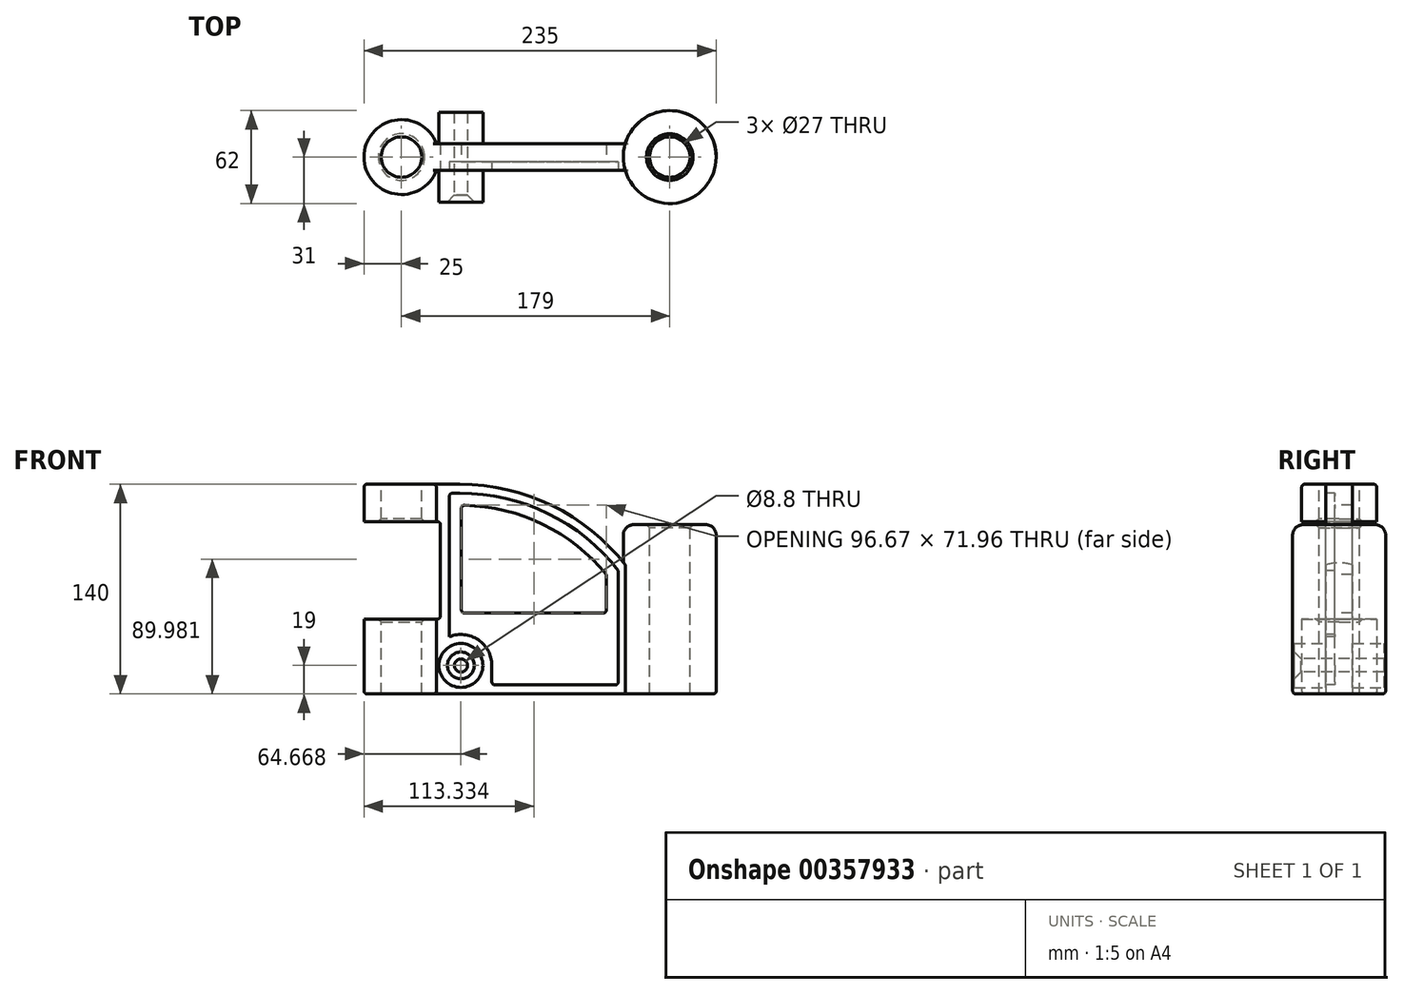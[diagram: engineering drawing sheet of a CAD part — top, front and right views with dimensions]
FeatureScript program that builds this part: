
annotation { "Feature Type Name" : "Feature", "Feature Type Description" : "" }
export const myFeature = defineFeature(function(context is Context, id is Id, definition is map)
    precondition{}
    {
        {
            assignVariable(context, id + "F0", {"name" : "A", "anyValue" : 140 * mm});
        }
        {
            assignVariable(context, id + "F1", {"name" : "B", "anyValue" : 62 * mm});
        }
        {
            assignVariable(context, id + "F2", {"name" : "Y", "anyValue" : (1.5 * getVariable(context, 'B')) + 20 * mm});
        }
        {
            var Q0;
            Q0=qCreatedBy(makeId("Top.planeOp"),FACE);
            var sketch = newSketch(context, id + "F3", { "sketchPlane" : qUnion([Q0])});
            skCircle(sketch, "E0", {"center": v(0, 0) * mm, "radius": 25 * mm});
            skSolve(sketch);
        }
        {
            var Q0;
            Q0 = qSketchRegion(id + "F3", true);
            extrude(context, id + "F4", {"entities" : qUnion([Q0]), "depth" : getVariable(context, 'A')});
        }
        {
            var Q0;
            Q0=qCreatedBy(makeId("Top.planeOp"),FACE);
            var sketch = newSketch(context, id + "F5", { "sketchPlane" : qUnion([Q0])});
            skCircle(sketch, "E1", {"center": v(179, 0) * mm, "radius": 31 * mm});
            skSolve(sketch);
        }
        {
            var Q0;
            Q0 = qSketchRegion(id + "F5", true);
            extrude(context, id + "F6", {"entities" : qUnion([Q0]), "depth" : getVariable(context, 'Y')});
        }
        {
            var Q0;
            Q0=qCreatedBy(makeId("Front.planeOp"),FACE);
            var sketch = newSketch(context, id + "F7", { "sketchPlane" : qUnion([Q0])});
            skLineSegment(sketch, "E2", {"start": v(39, 0) * mm, "end": v(39, 140.28) * mm, "construction": true});
            skLineSegment(sketch, "E3", {"start": v(179, 0) * mm, "end": v(179, 126.96) * mm, "construction": true});
            skArc(sketch, "E4", {"start": v(179, 0) * mm, "mid": v(138, 99) * mm, "end": v(39, 140) * mm});
            skLineSegment(sketch, "E5", {"start": v(39, 140) * mm, "end": v(0, 140) * mm});
            skLineSegment(sketch, "E6", {"start": v(0, 140) * mm, "end": v(0, 0) * mm});
            skLineSegment(sketch, "E7", {"start": v(0, 0) * mm, "end": v(179, 0) * mm});
            skSolve(sketch);
        }
        {
            var Q0;
            Q0 = qSketchRegion(id + "F7", true);
            extrude(context, id + "F8", {"entities" : qUnion([Q0]), "operationType" : NewBodyOperationType.ADD, "endBound" : BoundingType.SYMMETRIC, "depth" : 18 * mm});
        }
        {
            var Q0;
            Q0=makeQuery(id+"F8.boolean.opBoolean","MERGE",FACE,{"derivedFrom":[makeQuery(id+"F4.opExtrude","CAP_FACE",FACE,{"disambiguationData":[OSD([sQuery(id+"F3.wireOp",EDGE,"E0")])],"isStart":false}),makeQuery(id+"F8.opExtrude","SWEPT_FACE",FACE,{"disambiguationData":[OSD([sQuery(id+"F7.wireOp",EDGE,"E5")])]})]});
            var sketch = newSketch(context, id + "F9", { "sketchPlane" : qUnion([Q0])});
            skCircle(sketch, "E8", {"center": v(0, 0) * mm, "radius": 13.5 * mm});
            skCircle(sketch, "E9", {"center": v(179, 0) * mm, "radius": 13.5 * mm});
            skSolve(sketch);
        }
        {
            var Q0;
            Q0 = qSketchRegion(id + "F9", true);
            var Q1;
            Q1=makeQuery(id+"F8.boolean.opBoolean","MERGE",FACE,{"derivedFrom":[makeQuery(id+"F4.opExtrude","CAP_FACE",FACE,{"disambiguationData":[OSD([sQuery(id+"F3.wireOp",EDGE,"E0")])],"isStart":true}),makeQuery(id+"F6.opExtrude","CAP_FACE",FACE,{"disambiguationData":[OSD([sQuery(id+"F5.wireOp",EDGE,"E1")])],"isStart":true}),makeQuery(id+"F8.opExtrude","SWEPT_FACE",FACE,{"disambiguationData":[OSD([sQuery(id+"F7.wireOp",EDGE,"E7")])]})]});
            extrude(context, id + "F10", {"entities" : qUnion([Q0]), "operationType" : NewBodyOperationType.REMOVE, "endBound" : BoundingType.UP_TO_SURFACE, "oppositeDirection" : true, "endBoundEntityFace" : qUnion([Q1]), "depth" : 25 * mm});
        }
        {
            var Q0;
            Q0=makeQuery(id+"F8.opExtrude","CAP_FACE",FACE,{"disambiguationData":[OSD([sQuery(id+"F7.wireOp",EDGE,"E4"),sQuery(id+"F7.wireOp",EDGE,"E5"),sQuery(id+"F7.wireOp",EDGE,"E6"),sQuery(id+"F7.wireOp",EDGE,"E7")])],"isStart":false});
            var sketch = newSketch(context, id + "F11", { "sketchPlane" : qUnion([Q0])});
            skLineSegment(sketch, "E10.0", {"start": v(39, 134) * mm, "end": v(34, 134) * mm});
            skArc(sketch, "E10.1", {"start": v(144.67, 82.4) * mm, "mid": v(97.8, 120.41) * mm, "end": v(39, 134) * mm});
            skLineSegment(sketch, "E11.0", {"start": v(34, 6) * mm, "end": v(142.67, 6) * mm});
            skLineSegment(sketch, "E12", {"start": v(0, 0) * mm, "end": v(0, 142.94) * mm, "construction": true});
            skLineSegment(sketch, "E13", {"start": v(179.67, 0) * mm, "end": v(179.67, 122.02) * mm, "construction": true});
            skLineSegment(sketch, "E14", {"start": v(144.67, 8) * mm, "end": v(144.67, 82.4) * mm});
            skLineSegment(sketch, "E15", {"start": v(32, 8) * mm, "end": v(32, 132) * mm});
            skPoint(sketch, "E16.visualSharp", {"position": v(144.67, 6) * mm});
            skArc(sketch, "E16.filletArc", {"start": v(142.67, 6) * mm, "mid": v(144.08, 6.59) * mm, "end": v(144.67, 8) * mm});
            skPoint(sketch, "E17.visualSharp", {"position": v(32, 6) * mm});
            skArc(sketch, "E17.filletArc", {"start": v(32, 8) * mm, "mid": v(32.59, 6.59) * mm, "end": v(34, 6) * mm});
            skPoint(sketch, "E18.visualSharp", {"position": v(32, 134) * mm});
            skArc(sketch, "E18.filletArc", {"start": v(34, 134) * mm, "mid": v(32.59, 133.41) * mm, "end": v(32, 132) * mm});
            skSolve(sketch);
        }
        {
            var Q0;
            Q0=makeQuery(id+"F4.opExtrude","CAP_EDGE",EDGE,{"disambiguationData":[OSD([sQuery(id+"F3.wireOp",EDGE,"E0")])],"isStart":false});
            var Q1;
            Q1=makeQuery(id+"F4.opExtrude","CAP_EDGE",EDGE,{"disambiguationData":[OSD([sQuery(id+"F3.wireOp",EDGE,"E0")])],"isStart":true});
            var Q2;
            Q2=makeQuery(id+"F6.opExtrude","CAP_EDGE",EDGE,{"disambiguationData":[OSD([sQuery(id+"F5.wireOp",EDGE,"E1")])],"isStart":true});
            fillet(context, id + "F12", {"entities" : qUnion([Q0, Q1, Q2]), "radius" : 2 * mm, "tangentPropagation" : true, "allowEdgeOverflow" : false});
        }
        {
            var Q0;
            Q0=makeQuery(id+"F6.opExtrude","CAP_EDGE",EDGE,{"disambiguationData":[OSD([sQuery(id+"F5.wireOp",EDGE,"E1")])],"isStart":false});
            fillet(context, id + "F13", {"entities" : qUnion([Q0]), "radius" : 7 * mm, "tangentPropagation" : true, "allowEdgeOverflow" : false});
        }
        {
            var Q0;
            Q0=makeQuery(id+"F10.boolean.opBoolean","COPY",EDGE,{"derivedFrom":makeQuery(id+"F10.opExtrude","CAP_EDGE",EDGE,{"disambiguationData":[OSD([sQuery(id+"F9.wireOp",EDGE,"E8")])],"isStart":true})});
            var Q1;
            Q1=makeQuery(id+"F10.boolean.opBoolean","COPY",EDGE,{"derivedFrom":makeQuery(id+"F10.opExtrude","CAP_EDGE",EDGE,{"disambiguationData":[OSD([sQuery(id+"F9.wireOp",EDGE,"E8")])],"isStart":false})});
            var Q2;
            Q2=makeQuery(id+"F10.boolean.opBoolean","INTERSECT",EDGE,{"derivedFrom":[makeQuery(id+"F6.opExtrude","CAP_FACE",FACE,{"disambiguationData":[OSD([sQuery(id+"F5.wireOp",EDGE,"E1")])],"isStart":false}),makeQuery(id+"F10.opExtrude","SWEPT_FACE",FACE,{"disambiguationData":[OSD([sQuery(id+"F9.wireOp",EDGE,"E9")])]})]});
            var Q3;
            Q3=makeQuery(id+"F10.boolean.opBoolean","COPY",EDGE,{"derivedFrom":makeQuery(id+"F10.opExtrude","CAP_EDGE",EDGE,{"disambiguationData":[OSD([sQuery(id+"F9.wireOp",EDGE,"E9")])],"isStart":false})});
            chamfer(context, id + "F14", {"entities" : qUnion([Q0, Q1, Q2, Q3]), "width" : 2 * mm, "tangentPropagation" : true});
        }
        {
            var Q0;
            Q0=qCreatedBy(makeId("Front.planeOp"),FACE);
            var sketch = newSketch(context, id + "F15", { "sketchPlane" : qUnion([Q0])});
            skCircle(sketch, "E19", {"center": v(39.67, 19) * mm, "radius": 14.67 * mm});
            skSolve(sketch);
        }
        {
            var Q0;
            Q0 = qSketchRegion(id + "F15", true);
            extrude(context, id + "F16", {"entities" : qUnion([Q0]), "operationType" : NewBodyOperationType.ADD, "endBound" : BoundingType.SYMMETRIC, "depth" : 60 * mm});
        }
        {
            var Q0;
            Q0=makeQuery(id+"F11.imprint","IMPRINT",FACE,{"disambiguationData":[TD([[makeQuery(id+"F11.imprint","IMPRINT",EDGE,{"derivedFrom":sQuery(id+"F11.wireOp",EDGE,"E10.0")}),-1.0]])]});
            var sketch = newSketch(context, id + "F17", { "sketchPlane" : qUnion([Q0])});
            skLineSegment(sketch, "E20.0.0", {"start": v(32, 132) * mm, "end": v(32, 38.2) * mm});
            skLineSegment(sketch, "E20.0.2", {"start": v(62.34, 6) * mm, "end": v(142.67, 6) * mm});
            skArc(sketch, "E20.0.3", {"start": v(142.67, 6) * mm, "mid": v(144.08, 6.59) * mm, "end": v(144.67, 8) * mm});
            skLineSegment(sketch, "E20.0.4", {"start": v(144.67, 8) * mm, "end": v(144.67, 82.4) * mm});
            skArc(sketch, "E20.0.5", {"start": v(144.67, 82.4) * mm, "mid": v(97.8, 120.41) * mm, "end": v(39, 134) * mm});
            skLineSegment(sketch, "E20.0.6", {"start": v(39, 134) * mm, "end": v(34, 134) * mm});
            skArc(sketch, "E20.0.7", {"start": v(34, 134) * mm, "mid": v(32.59, 133.41) * mm, "end": v(32, 132) * mm});
            skArc(sketch, "E21.0", {"start": v(60.34, 19) * mm, "mid": v(51.26, 36.11) * mm, "end": v(32, 38.2) * mm});
            skPoint(sketch, "E20.0.1.end.orphan", {"position": v(34, 6) * mm});
            skPoint(sketch, "E20.0.1.start.orphan", {"position": v(32, 8) * mm});
            skLineSegment(sketch, "E22", {"start": v(60.34, 19) * mm, "end": v(60.34, 8) * mm});
            skPoint(sketch, "E23.visualSharp", {"position": v(60.34, 6) * mm});
            skArc(sketch, "E23.filletArc", {"start": v(60.34, 8) * mm, "mid": v(60.92, 6.59) * mm, "end": v(62.34, 6) * mm});
            skSolve(sketch);
        }
        {
            var Q0;
            Q0 = qSketchRegion(id + "F17", true);
            extrude(context, id + "F18", {"entities" : qUnion([Q0]), "operationType" : NewBodyOperationType.REMOVE, "oppositeDirection" : true, "depth" : 6 * mm});
        }
        {
            var Q0;
            Q0=makeQuery(id+"F16.opExtrude","CAP_FACE",FACE,{"disambiguationData":[OSD([sQuery(id+"F15.wireOp",EDGE,"E19")])],"isStart":false});
            var sketch = newSketch(context, id + "F19", { "sketchPlane" : qUnion([Q0])});
            skPoint(sketch, "E24", {"position": v(39.67, 19) * mm});
            skSolve(sketch);
        }
        {
            var Q0;
            Q0=sQuery(id+"F19.wireOp",VERTEX,"E24");
            var Q1;
            Q1=makeQuery(id+"F4.opExtrude","SWEPT_BODY",BODY,{"disambiguationData":[OSD([sQuery(id+"F3.wireOp",EDGE,"E0")])]});
            hole(context, id + "F20", {"style" : HoleStyle.C_SINK, "endStyle" : HoleEndStyle.THROUGH, "standardTappedOrClearance" : lookupTablePath({ "standard" : "ISO", "fit" : "Normal", "size" : "M8", "type" : "Clearance" }), "standardBlindInLast" : lookupTablePath({ "fit" : "Standard", "standard" : "ISO", "size" : "M8", "type" : "Clearance" }), "holeDiameter" : 8.8 * mm, "cSinkDiameter" : 17.92 * mm, "cSinkAngle" : 90 * degree, "isTappedThrough" : true, "tappedDepth" : 12 * mm, "tapClearance" : 3, "locations" : qUnion([Q0]), "scope" : qUnion([Q1])});
        }
        {
            var Q0;
            Q0=makeQuery(id+"F17.imprint","IMPRINT",FACE,{"disambiguationData":[TD([[makeQuery(id+"F17.imprint","IMPRINT",EDGE,{"derivedFrom":sQuery(id+"F17.wireOp",EDGE,"E20.0.0")}),-1.0]])]});
            var sketch = newSketch(context, id + "F21", { "sketchPlane" : qUnion([Q0])});
            skLineSegment(sketch, "E25.0", {"start": v(136.67, 56) * mm, "end": v(136.67, 79.6) * mm});
            skArc(sketch, "E25.1", {"start": v(136.67, 79.6) * mm, "mid": v(94.44, 113.15) * mm, "end": v(42.05, 125.96) * mm});
            skLineSegment(sketch, "E25.3", {"start": v(40, 56) * mm, "end": v(40, 123.96) * mm});
            skLineSegment(sketch, "E26.0", {"start": v(42, 54) * mm, "end": v(134.67, 54) * mm});
            skPoint(sketch, "E27.visualSharp", {"position": v(68.34, 54) * mm});
            skPoint(sketch, "E28.visualSharp", {"position": v(40, 47.67) * mm});
            skPoint(sketch, "E29.visualSharp", {"position": v(136.67, 54) * mm});
            skArc(sketch, "E29.filletArc", {"start": v(134.67, 54) * mm, "mid": v(136.08, 54.59) * mm, "end": v(136.67, 56) * mm});
            skArc(sketch, "E30.filletArc", {"start": v(42.05, 125.96) * mm, "mid": v(40.6, 125.4) * mm, "end": v(40, 123.96) * mm});
            skPoint(sketch, "E31.visualSharp", {"position": v(40, 54) * mm});
            skArc(sketch, "E31.filletArc", {"start": v(40, 56) * mm, "mid": v(40.59, 54.59) * mm, "end": v(42, 54) * mm});
            skSolve(sketch);
        }
        {
            var Q0;
            Q0 = qSketchRegion(id + "F21", true);
            extrude(context, id + "F22", {"entities" : qUnion([Q0]), "operationType" : NewBodyOperationType.REMOVE, "endBound" : BoundingType.THROUGH_ALL, "oppositeDirection" : true, "depth" : 25 * mm});
        }
        {
            var Q0;
            Q0=qCreatedBy(makeId("Front.planeOp"),FACE);
            var sketch = newSketch(context, id + "F23", { "sketchPlane" : qUnion([Q0])});
            skLineSegment(sketch, "E32.bottom", {"start": v(-34.15, 50) * mm, "end": v(24, 50) * mm});
            skLineSegment(sketch, "E32.top", {"start": v(-34.15, 115) * mm, "end": v(24, 115) * mm});
            skLineSegment(sketch, "E32.left", {"start": v(-34.15, 50) * mm, "end": v(-34.15, 115) * mm});
            skLineSegment(sketch, "E32.right", {"start": v(26, 52) * mm, "end": v(26, 113) * mm});
            skPoint(sketch, "E33.visualSharp", {"position": v(26, 115) * mm});
            skArc(sketch, "E33.filletArc", {"start": v(26, 113) * mm, "mid": v(25.41, 114.41) * mm, "end": v(24, 115) * mm});
            skPoint(sketch, "E34.visualSharp", {"position": v(26, 50) * mm});
            skArc(sketch, "E34.filletArc", {"start": v(24, 50) * mm, "mid": v(25.41, 50.59) * mm, "end": v(26, 52) * mm});
            skSolve(sketch);
        }
        {
            var Q0;
            Q0 = qSketchRegion(id + "F23", true);
            extrude(context, id + "F24", {"entities" : qUnion([Q0]), "operationType" : NewBodyOperationType.REMOVE, "endBound" : BoundingType.THROUGH_ALL, "oppositeDirection" : true, "depth" : 25 * mm, "hasSecondDirection" : true, "secondDirectionOppositeDirection" : false, "secondDirectionDepth" : 25 * mm});
        }
        {
            var Q0;
            Q0=makeQuery(id+"F24.boolean.opBoolean","INTERSECT",EDGE,{"derivedFrom":[makeQuery(id+"F10.boolean.opBoolean","COPY",FACE,{"derivedFrom":makeQuery(id+"F10.opExtrude","SWEPT_FACE",FACE,{"disambiguationData":[OSD([sQuery(id+"F9.wireOp",EDGE,"E8")])]})}),makeQuery(id+"F24.opExtrude","SWEPT_FACE",FACE,{"disambiguationData":[OSD([sQuery(id+"F23.wireOp",EDGE,"E32.bottom")])]})]});
            var Q1;
            Q1=makeQuery(id+"F24.boolean.opBoolean","INTERSECT",EDGE,{"derivedFrom":[makeQuery(id+"F10.boolean.opBoolean","COPY",FACE,{"derivedFrom":makeQuery(id+"F10.opExtrude","SWEPT_FACE",FACE,{"disambiguationData":[OSD([sQuery(id+"F9.wireOp",EDGE,"E8")])]})}),makeQuery(id+"F24.opExtrude","SWEPT_FACE",FACE,{"disambiguationData":[OSD([sQuery(id+"F23.wireOp",EDGE,"E32.top")])]})]});
            chamfer(context, id + "F25", {"entities" : qUnion([Q0, Q1]), "width" : 2 * mm, "tangentPropagation" : true});
        }
    });
